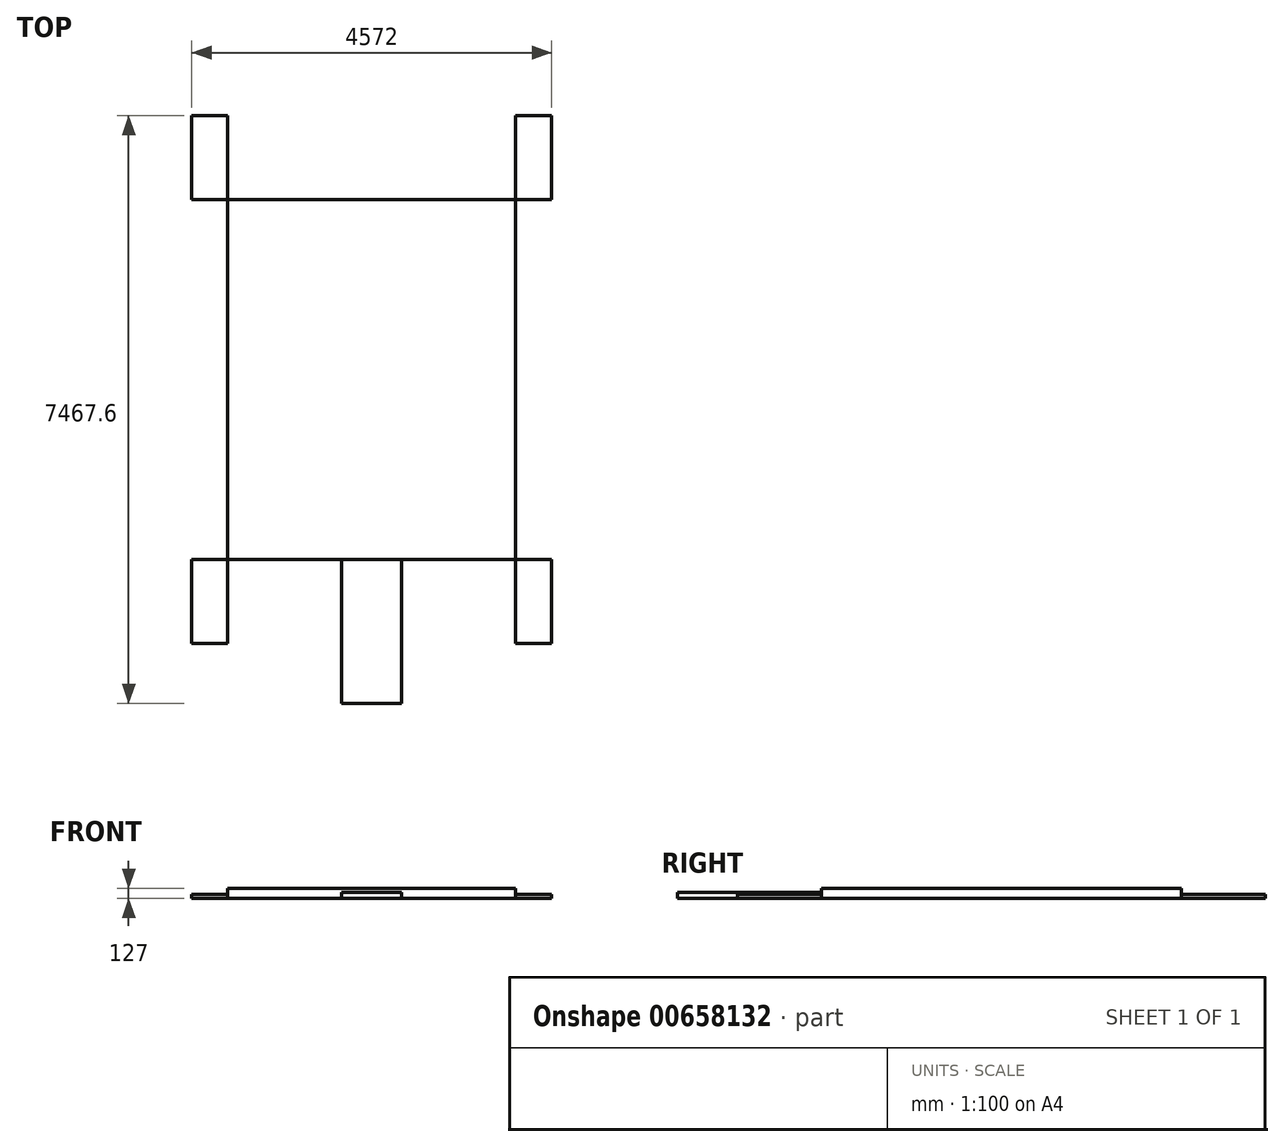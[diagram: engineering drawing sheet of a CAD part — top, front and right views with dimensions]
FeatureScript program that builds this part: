
annotation { "Feature Type Name" : "Feature", "Feature Type Description" : "" }
export const myFeature = defineFeature(function(context is Context, id is Id, definition is map)
    precondition{}
    {
        {
            var Q0;
            Q0=qCreatedBy(makeId("Top.planeOp"),FACE);
            var sketch = newSketch(context, id + "F0", { "sketchPlane" : qUnion([Q0])});
            skLineSegment(sketch, "E0.bottom", {"start": v(0, 0) * mm, "end": v(3657.6, 0) * mm});
            skLineSegment(sketch, "E0.top", {"start": v(0, 4572) * mm, "end": v(3657.6, 4572) * mm});
            skLineSegment(sketch, "E0.left", {"start": v(0, 0) * mm, "end": v(0, 4572) * mm});
            skLineSegment(sketch, "E0.right", {"start": v(3657.6, 0) * mm, "end": v(3657.6, 4572) * mm});
            skSolve(sketch);
        }
        {
            var Q0;
            Q0 = qSketchRegion(id + "F0", true);
            extrude(context, id + "F1", {"entities" : qUnion([Q0]), "depth" : 127 * mm, "offsetDistance" : 25.4 * mm});
        }
        {
            var Q0;
            Q0=makeQuery(id+"F1.opExtrude","CAP_FACE",FACE,{"disambiguationData":[OSD([sQuery(id+"F0.wireOp",EDGE,"E0.bottom"),sQuery(id+"F0.wireOp",EDGE,"E0.top"),sQuery(id+"F0.wireOp",EDGE,"E0.left"),sQuery(id+"F0.wireOp",EDGE,"E0.right")])],"isStart":false});
            var sketch = newSketch(context, id + "F2", { "sketchPlane" : qUnion([Q0])});
            skPoint(sketch, "E1", {"position": v(1447.8, 0) * mm});
            skPoint(sketch, "E2", {"position": v(2209.8, -1830.02) * mm});
            skPoint(sketch, "E3", {"position": v(1447.8, -1828.8) * mm});
            skLineSegment(sketch, "E4.bottom", {"start": v(1447.8, -1828.8) * mm, "end": v(2209.8, -1828.8) * mm});
            skLineSegment(sketch, "E4.top", {"start": v(1447.8, 0) * mm, "end": v(2209.8, 0) * mm});
            skLineSegment(sketch, "E4.left", {"start": v(1447.8, -1828.8) * mm, "end": v(1447.8, 0) * mm});
            skLineSegment(sketch, "E4.right", {"start": v(2209.8, -1828.8) * mm, "end": v(2209.8, 0) * mm});
            skSolve(sketch);
        }
        {
            var Q0;
            Q0 = qSketchRegion(id + "F2", true);
            extrude(context, id + "F3", {"entities" : qUnion([Q0]), "oppositeDirection" : true, "depth" : 127 * mm, "offsetDistance" : 25.4 * mm, "hasSecondDirection" : true, "secondDirectionOppositeDirection" : true, "secondDirectionDepth" : 50.8 * mm});
        }
        {
            var Q0;
            Q0=makeQuery(id+"F1.opExtrude","CAP_FACE",FACE,{"disambiguationData":[OSD([sQuery(id+"F0.wireOp",EDGE,"E0.bottom"),sQuery(id+"F0.wireOp",EDGE,"E0.top"),sQuery(id+"F0.wireOp",EDGE,"E0.left"),sQuery(id+"F0.wireOp",EDGE,"E0.right")])],"isStart":false});
            var sketch = newSketch(context, id + "F4", { "sketchPlane" : qUnion([Q0])});
            skLineSegment(sketch, "E5.bottom", {"start": v(0, 0) * mm, "end": v(-457.2, 0) * mm});
            skLineSegment(sketch, "E5.top", {"start": v(0, -1066.8) * mm, "end": v(-457.2, -1066.8) * mm});
            skLineSegment(sketch, "E5.left", {"start": v(0, 0) * mm, "end": v(0, -1066.8) * mm});
            skLineSegment(sketch, "E5.right", {"start": v(-457.2, 0) * mm, "end": v(-457.2, -1066.8) * mm});
            skLineSegment(sketch, "E6.bottom", {"start": v(3657.6, 0) * mm, "end": v(4114.8, 0) * mm});
            skLineSegment(sketch, "E6.top", {"start": v(3657.6, -1066.8) * mm, "end": v(4114.8, -1066.8) * mm});
            skLineSegment(sketch, "E6.left", {"start": v(3657.6, 0) * mm, "end": v(3657.6, -1066.8) * mm});
            skLineSegment(sketch, "E6.right", {"start": v(4114.8, 0) * mm, "end": v(4114.8, -1066.8) * mm});
            skSolve(sketch);
        }
        {
            var Q0;
            Q0 = qSketchRegion(id + "F4", true);
            extrude(context, id + "F5", {"entities" : qUnion([Q0]), "oppositeDirection" : true, "depth" : 127 * mm, "offsetDistance" : 25.4 * mm, "hasSecondDirection" : true, "secondDirectionOppositeDirection" : true, "secondDirectionDepth" : 76.2 * mm});
        }
        {
            var Q0;
            Q0=makeQuery(id+"F1.opExtrude","CAP_FACE",FACE,{"disambiguationData":[OSD([sQuery(id+"F0.wireOp",EDGE,"E0.bottom"),sQuery(id+"F0.wireOp",EDGE,"E0.top"),sQuery(id+"F0.wireOp",EDGE,"E0.left"),sQuery(id+"F0.wireOp",EDGE,"E0.right")])],"isStart":false});
            var sketch = newSketch(context, id + "F6", { "sketchPlane" : qUnion([Q0])});
            skLineSegment(sketch, "E7.bottom", {"start": v(3657.6, 4572) * mm, "end": v(4114.8, 4572) * mm});
            skLineSegment(sketch, "E7.top", {"start": v(3657.6, 5638.8) * mm, "end": v(4114.8, 5638.8) * mm});
            skLineSegment(sketch, "E7.left", {"start": v(3657.6, 4572) * mm, "end": v(3657.6, 5638.8) * mm});
            skLineSegment(sketch, "E7.right", {"start": v(4114.8, 4572) * mm, "end": v(4114.8, 5638.8) * mm});
            skLineSegment(sketch, "E8.bottom", {"start": v(0, 4572) * mm, "end": v(-457.2, 4572) * mm});
            skLineSegment(sketch, "E8.top", {"start": v(0, 5638.8) * mm, "end": v(-457.2, 5638.8) * mm});
            skLineSegment(sketch, "E8.left", {"start": v(0, 4572) * mm, "end": v(0, 5638.8) * mm});
            skLineSegment(sketch, "E8.right", {"start": v(-457.2, 4572) * mm, "end": v(-457.2, 5638.8) * mm});
            skSolve(sketch);
        }
        {
            var Q0;
            Q0 = qSketchRegion(id + "F6", true);
            extrude(context, id + "F7", {"entities" : qUnion([Q0]), "oppositeDirection" : true, "depth" : 127 * mm, "offsetDistance" : 25.4 * mm, "hasSecondDirection" : true, "secondDirectionOppositeDirection" : true, "secondDirectionDepth" : 76.2 * mm});
        }
    });
